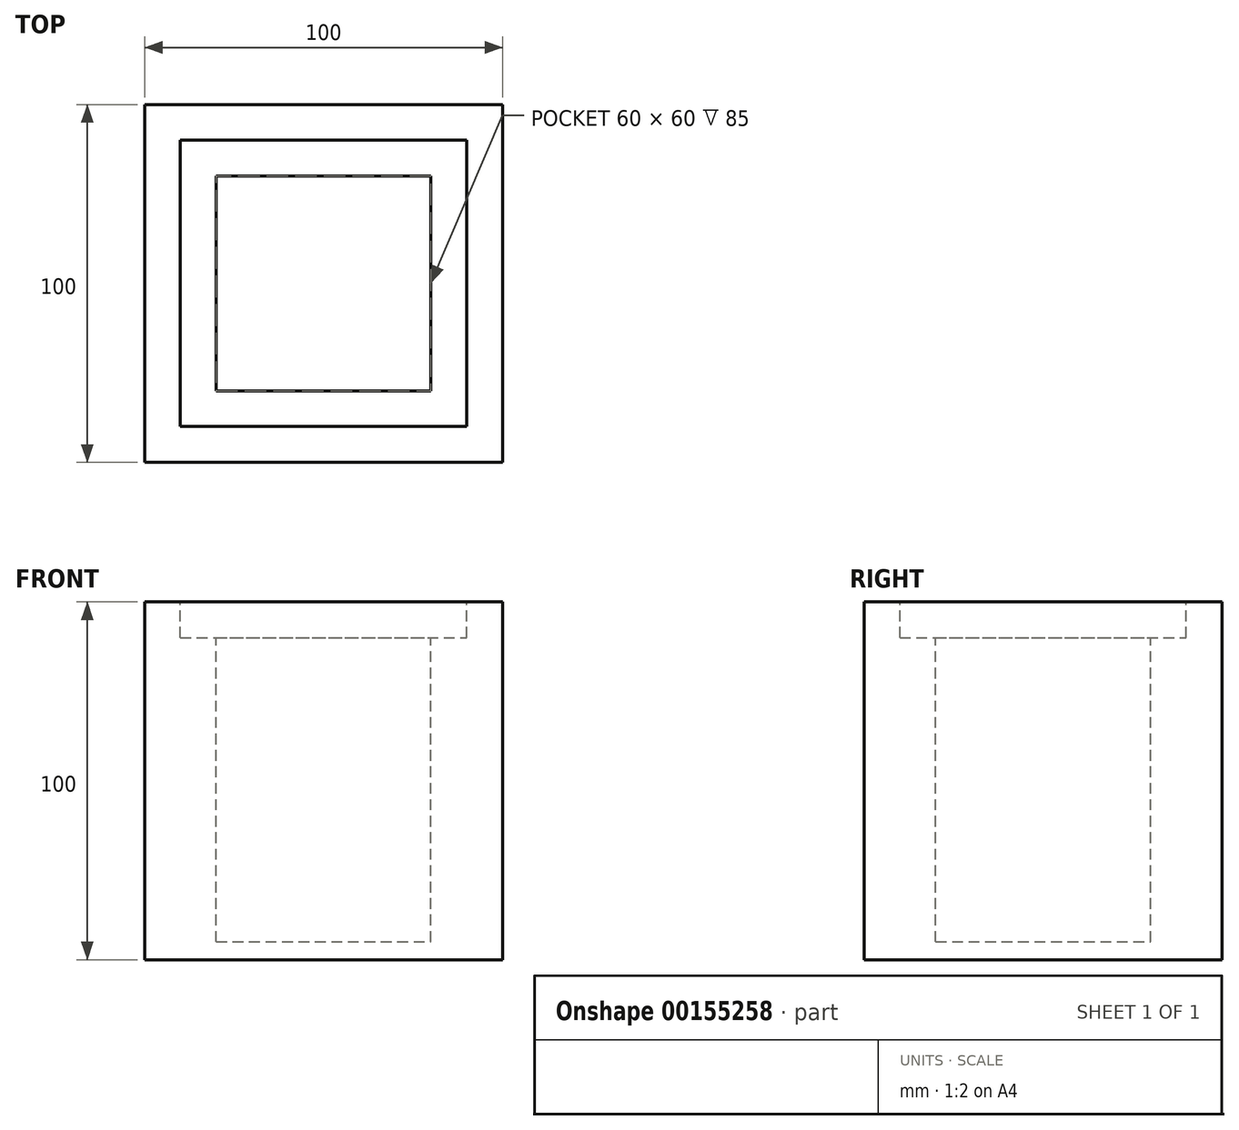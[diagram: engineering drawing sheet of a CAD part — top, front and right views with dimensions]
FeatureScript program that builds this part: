
annotation { "Feature Type Name" : "Feature", "Feature Type Description" : "" }
export const myFeature = defineFeature(function(context is Context, id is Id, definition is map)
    precondition{}
    {
        {
            var Q0;
            Q0=qCreatedBy(makeId("Top.planeOp"),FACE);
            var sketch = newSketch(context, id + "F0", { "sketchPlane" : qUnion([Q0])});
            skLineSegment(sketch, "E0.bottom", {"start": v(-50, -50) * mm, "end": v(50, -50) * mm});
            skLineSegment(sketch, "E0.top", {"start": v(-50, 50) * mm, "end": v(50, 50) * mm});
            skLineSegment(sketch, "E0.left", {"start": v(-50, -50) * mm, "end": v(-50, 50) * mm});
            skLineSegment(sketch, "E0.right", {"start": v(50, -50) * mm, "end": v(50, 50) * mm});
            skPoint(sketch, "E0.middle", {"position": v(0, 0) * mm});
            skSolve(sketch);
        }
        {
            var Q0;
            Q0=makeQuery(id+"F0.imprint","IMPRINT",FACE,{"disambiguationData":[TD([[makeQuery(id+"F0.imprint","IMPRINT",EDGE,{"derivedFrom":sQuery(id+"F0.wireOp",EDGE,"E0.bottom")}),1.0]])]});
            extrude(context, id + "F1", {"entities" : qUnion([Q0]), "depth" : 100 * mm});
        }
        {
            var Q0;
            Q0=makeQuery(id+"F1.opExtrude","CAP_FACE",FACE,{"disambiguationData":[OSD([sQuery(id+"F0.wireOp",EDGE,"E0.bottom"),sQuery(id+"F0.wireOp",EDGE,"E0.top"),sQuery(id+"F0.wireOp",EDGE,"E0.left"),sQuery(id+"F0.wireOp",EDGE,"E0.right")])],"isStart":false});
            var sketch = newSketch(context, id + "F2", { "sketchPlane" : qUnion([Q0])});
            skLineSegment(sketch, "E1.bottom", {"start": v(-30, -30) * mm, "end": v(30, -30) * mm});
            skLineSegment(sketch, "E1.top", {"start": v(-30, 30) * mm, "end": v(30, 30) * mm});
            skLineSegment(sketch, "E1.left", {"start": v(-30, -30) * mm, "end": v(-30, 30) * mm});
            skLineSegment(sketch, "E1.right", {"start": v(30, -30) * mm, "end": v(30, 30) * mm});
            skPoint(sketch, "E1.middle", {"position": v(0, 0) * mm});
            skSolve(sketch);
        }
        {
            var Q0;
            Q0=makeQuery(id+"F2.imprint","IMPRINT",FACE,{"disambiguationData":[TD([[makeQuery(id+"F2.imprint","IMPRINT",EDGE,{"derivedFrom":sQuery(id+"F2.wireOp",EDGE,"E1.bottom")}),1.0]])]});
            extrude(context, id + "F3", {"entities" : qUnion([Q0]), "operationType" : NewBodyOperationType.REMOVE, "oppositeDirection" : true, "depth" : 95 * mm});
        }
        {
            var Q0;
            Q0=makeQuery(id+"F1.opExtrude","CAP_FACE",FACE,{"disambiguationData":[OSD([sQuery(id+"F0.wireOp",EDGE,"E0.bottom"),sQuery(id+"F0.wireOp",EDGE,"E0.top"),sQuery(id+"F0.wireOp",EDGE,"E0.left"),sQuery(id+"F0.wireOp",EDGE,"E0.right")])],"isStart":false});
            var sketch = newSketch(context, id + "F4", { "sketchPlane" : qUnion([Q0])});
            skLineSegment(sketch, "E2.bottom", {"start": v(-40, -40) * mm, "end": v(40, -40) * mm});
            skLineSegment(sketch, "E2.top", {"start": v(-40, 40) * mm, "end": v(40, 40) * mm});
            skLineSegment(sketch, "E2.left", {"start": v(-40, -40) * mm, "end": v(-40, 40) * mm});
            skLineSegment(sketch, "E2.right", {"start": v(40, -40) * mm, "end": v(40, 40) * mm});
            skPoint(sketch, "E2.middle", {"position": v(0, 0) * mm});
            skSolve(sketch);
        }
        {
            var Q0;
            Q0=makeQuery(id+"F4.imprint","IMPRINT",FACE,{"disambiguationData":[TD([[makeQuery(id+"F4.imprint","IMPRINT",EDGE,{"derivedFrom":sQuery(id+"F4.wireOp",EDGE,"E2.bottom")}),1.0]])]});
            extrude(context, id + "F5", {"entities" : qUnion([Q0]), "operationType" : NewBodyOperationType.REMOVE, "oppositeDirection" : true, "depth" : 10 * mm});
        }
    });
